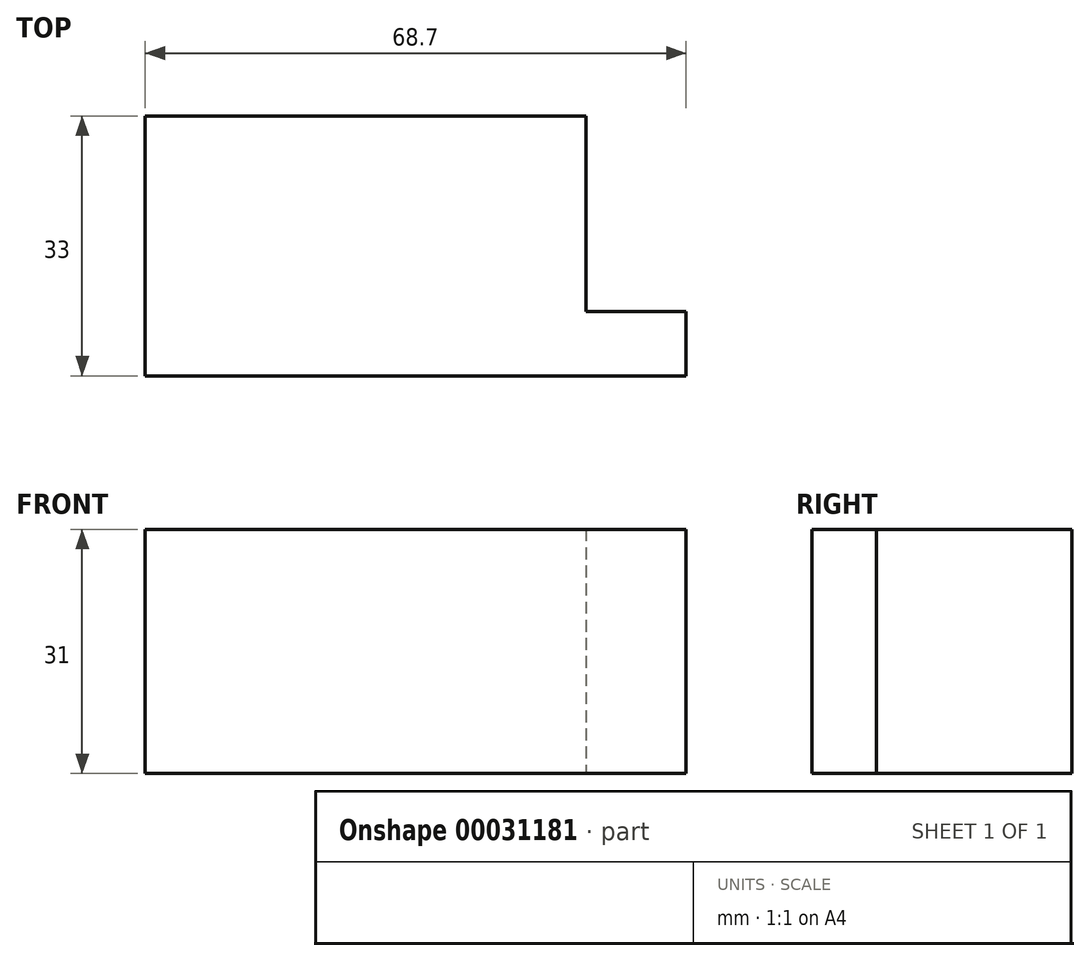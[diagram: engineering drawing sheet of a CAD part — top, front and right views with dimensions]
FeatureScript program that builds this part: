
annotation { "Feature Type Name" : "Feature", "Feature Type Description" : "" }
export const myFeature = defineFeature(function(context is Context, id is Id, definition is map)
    precondition{}
    {
        {
            var Q0;
            Q0=qCreatedBy(makeId("Right.planeOp"),FACE);
            var sketch = newSketch(context, id + "F0", { "sketchPlane" : qUnion([Q0])});
            skLineSegment(sketch, "E0.bottom", {"start": v(0, 0) * mm, "end": v(33, 0) * mm});
            skLineSegment(sketch, "E0.top", {"start": v(0, 31) * mm, "end": v(33, 31) * mm});
            skLineSegment(sketch, "E0.left", {"start": v(0, 0) * mm, "end": v(0, 31) * mm});
            skLineSegment(sketch, "E0.right", {"start": v(33, 0) * mm, "end": v(33, 31) * mm});
            skSolve(sketch);
        }
        {
            var Q0;
            Q0 = qSketchRegion(id + "F0", true);
            extrude(context, id + "F1", {"entities" : qUnion([Q0]), "depth" : 56 * mm});
        }
        {
            var Q0;
            Q0=makeQuery(id+"F1.opExtrude","CAP_FACE",FACE,{"disambiguationData":[OSD([sQuery(id+"F0.wireOp",EDGE,"E0.bottom"),sQuery(id+"F0.wireOp",EDGE,"E0.top"),sQuery(id+"F0.wireOp",EDGE,"E0.left"),sQuery(id+"F0.wireOp",EDGE,"E0.right")])],"isStart":false});
            var sketch = newSketch(context, id + "F2", { "sketchPlane" : qUnion([Q0])});
            skLineSegment(sketch, "E1.bottom", {"start": v(0, 31) * mm, "end": v(8.19, 31) * mm});
            skLineSegment(sketch, "E1.top", {"start": v(0, 0) * mm, "end": v(8.19, 0) * mm});
            skLineSegment(sketch, "E1.left", {"start": v(0, 31) * mm, "end": v(0, 0) * mm});
            skLineSegment(sketch, "E1.right", {"start": v(8.19, 31) * mm, "end": v(8.19, 0) * mm});
            skSolve(sketch);
        }
        {
            var Q0;
            Q0 = qSketchRegion(id + "F2", true);
            extrude(context, id + "F3", {"entities" : qUnion([Q0]), "operationType" : NewBodyOperationType.ADD, "depth" : 12.7 * mm});
        }
    });
